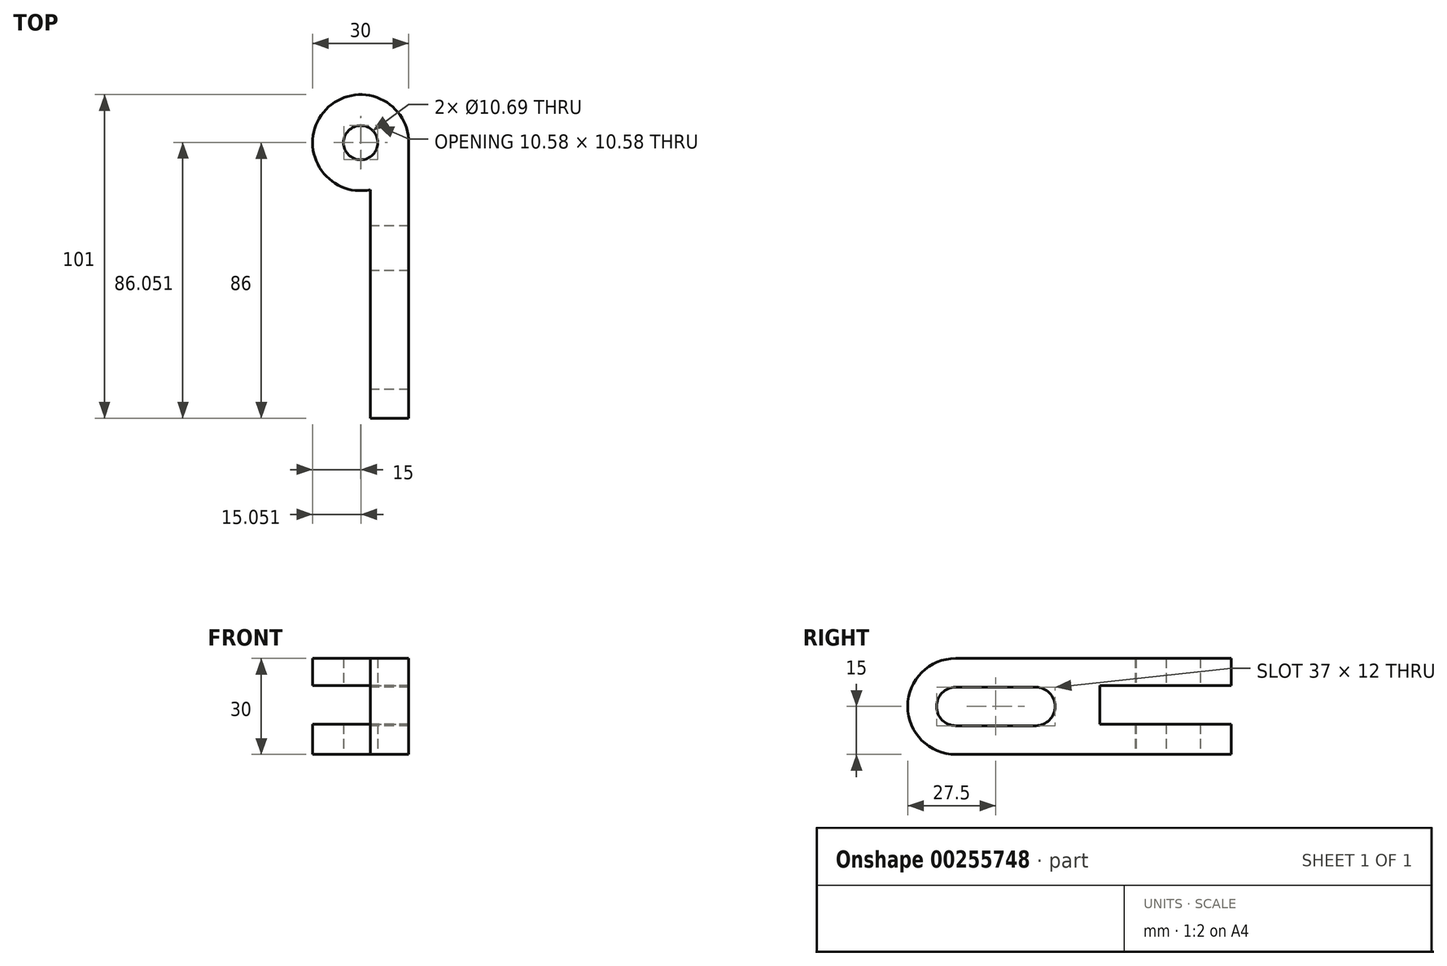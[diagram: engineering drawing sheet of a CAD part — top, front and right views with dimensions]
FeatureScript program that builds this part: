
annotation { "Feature Type Name" : "Feature", "Feature Type Description" : "" }
export const myFeature = defineFeature(function(context is Context, id is Id, definition is map)
    precondition{}
    {
        {
            var Q0;
            Q0=qCreatedBy(makeId("Top.planeOp"),FACE);
            var sketch = newSketch(context, id + "F0", { "sketchPlane" : qUnion([Q0])});
            skCircle(sketch, "E0", {"center": v(0, 0) * mm, "radius": 5.34 * mm});
            skArc(sketch, "E1", {"start": v(15, 0) * mm, "mid": v(-11.62, 9.49) * mm, "end": v(3, -14.7) * mm});
            skLineSegment(sketch, "E2.top", {"start": v(3, -86) * mm, "end": v(15, -86) * mm});
            skLineSegment(sketch, "E2.right", {"start": v(15, 0) * mm, "end": v(15, -86) * mm});
            skLineSegment(sketch, "E3.trimOffspring", {"start": v(3, -14.7) * mm, "end": v(3, -86) * mm});
            skSolve(sketch);
        }
        {
            var Q0;
            Q0=makeQuery(id+"F0.imprint","IMPRINT",FACE,{"disambiguationData":[TD([[makeQuery(id+"F0.imprint","IMPRINT",EDGE,{"derivedFrom":sQuery(id+"F0.wireOp",EDGE,"E0")}),-1.0]])]});
            extrude(context, id + "F1", {"entities" : qUnion([Q0]), "endBound" : BoundingType.SYMMETRIC, "depth" : 30 * mm});
        }
        {
            var Q0;
            Q0=qCreatedBy(makeId("Right.planeOp"),FACE);
            cPlane(context, id + "F2", {"entities" : qUnion([Q0]), "cplaneType" : CPlaneType.OFFSET, "offset" : 47.1 * mm, "oppositeDirection" : true, "width" : 150 * mm, "height" : 150 * mm});
        }
        {
            var Q0;
            Q0=qCreatedBy(id+"F2.planeOp",FACE);
            var sketch = newSketch(context, id + "F3", { "sketchPlane" : qUnion([Q0])});
            skLineSegment(sketch, "E4.bottom", {"start": v(15, -5.55) * mm, "end": v(-26, -5.55) * mm});
            skLineSegment(sketch, "E4.top", {"start": v(15, 6.45) * mm, "end": v(-26, 6.45) * mm});
            skLineSegment(sketch, "E4.left", {"start": v(15, -5.55) * mm, "end": v(15, 6.45) * mm});
            skLineSegment(sketch, "E4.right", {"start": v(-26, -5.55) * mm, "end": v(-26, 6.45) * mm});
            skLineSegment(sketch, "E5.bottom", {"start": v(-46, -6) * mm, "end": v(-71, -6) * mm});
            skLineSegment(sketch, "E5.top", {"start": v(-46, 6) * mm, "end": v(-71, 6) * mm});
            skArc(sketch, "E6", {"start": v(-46, -6) * mm, "mid": v(-40, 0) * mm, "end": v(-46, 6) * mm});
            skArc(sketch, "E7", {"start": v(-71, -6) * mm, "mid": v(-77, 0) * mm, "end": v(-71, 6) * mm});
            skLineSegment(sketch, "E8.0", {"start": v(-14.7, -15) * mm, "end": v(-86, -15) * mm});
            skLineSegment(sketch, "E9.0", {"start": v(-14.7, 15) * mm, "end": v(-86, 15) * mm});
            skLineSegment(sketch, "E10.0", {"start": v(-86, 15) * mm, "end": v(-86, -15) * mm});
            skArc(sketch, "E11", {"start": v(-71, -15) * mm, "mid": v(-86, 0) * mm, "end": v(-71, 15) * mm});
            skLineSegment(sketch, "E12", {"start": v(15, 15) * mm, "end": v(15, -15) * mm});
            skSolve(sketch);
        }
        {
            var Q0;
            {var subQ0=sQuery(id+"F3.wireOp",EDGE,"E4.bottom");Q0=makeQuery(id+"F3.imprint","IMPRINT",FACE,{"disambiguationData":[TD([[makeQuery(id+"F3.imprint","IMPRINT",EDGE,{"derivedFrom":subQ0}),-1.0]])]});}
            var Q1;
            Q1=makeQuery(id+"F3.imprint","IMPRINT",FACE,{"disambiguationData":[TD([[makeQuery(id+"F3.imprint","IMPRINT",EDGE,{"derivedFrom":sQuery(id+"F3.wireOp",EDGE,"E5.bottom")}),-1.0]])]});
            var Q2;
            {var subQ0=sQuery(id+"F3.wireOp",EDGE,"E10.0");var subQ1=sQuery(id+"F3.wireOp",EDGE,"E8.0");var subQ2=makeQuery(id+"F3.imprint","INTERSECT",VERTEX,{"derivedFrom":[subQ1,subQ0]});Q2=makeQuery(id+"F3.imprint","IMPRINT",FACE,{"disambiguationData":[TD([[makeQuery(id+"F3.imprint","IMPRINT",EDGE,{"disambiguationData":[TD([[subQ2,1.0]])],"derivedFrom":subQ1}),-1.0]])]});}
            var Q3;
            {var subQ0=sQuery(id+"F3.wireOp",EDGE,"E10.0");var subQ1=sQuery(id+"F3.wireOp",EDGE,"E9.0");var subQ2=makeQuery(id+"F3.imprint","INTERSECT",VERTEX,{"derivedFrom":[subQ1,subQ0]});Q3=makeQuery(id+"F3.imprint","IMPRINT",FACE,{"disambiguationData":[TD([[makeQuery(id+"F3.imprint","IMPRINT",EDGE,{"disambiguationData":[TD([[subQ2,1.0]])],"derivedFrom":subQ1}),1.0]])]});}
            extrude(context, id + "F4", {"entities" : qUnion([Q0, Q1, Q2, Q3]), "operationType" : NewBodyOperationType.REMOVE, "endBound" : BoundingType.THROUGH_ALL, "depth" : 25 * mm});
        }
    });
